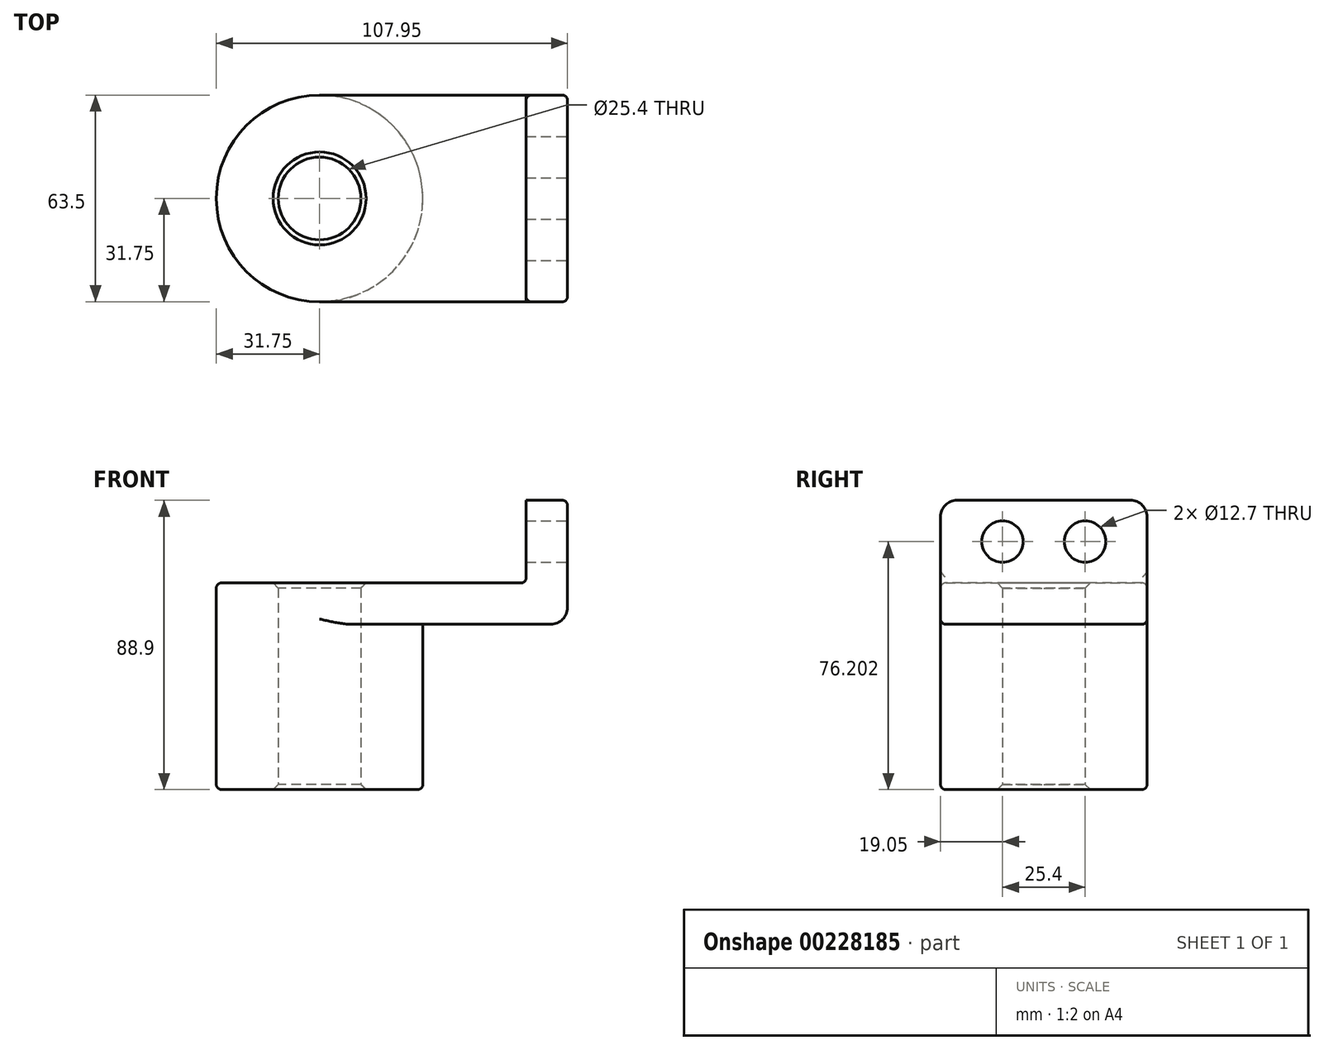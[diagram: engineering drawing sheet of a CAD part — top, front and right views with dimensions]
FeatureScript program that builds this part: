
annotation { "Feature Type Name" : "Feature", "Feature Type Description" : "" }
export const myFeature = defineFeature(function(context is Context, id is Id, definition is map)
    precondition{}
    {
        {
            var Q0;
            Q0=qCreatedBy(makeId("Top.planeOp"),FACE);
            var sketch = newSketch(context, id + "F0", { "sketchPlane" : qUnion([Q0])});
            skLineSegment(sketch, "E0.bottom", {"start": v(-38.1, 31.75) * mm, "end": v(38.1, 31.75) * mm});
            skLineSegment(sketch, "E0.top", {"start": v(-38.1, -31.75) * mm, "end": v(38.1, -31.75) * mm});
            skLineSegment(sketch, "E0.left", {"start": v(-38.1, 31.75) * mm, "end": v(-38.1, -31.75) * mm});
            skLineSegment(sketch, "E0.right", {"start": v(38.1, 31.75) * mm, "end": v(38.1, -31.75) * mm});
            skPoint(sketch, "E0.middle", {"position": v(0, 0) * mm});
            skCircle(sketch, "E1", {"center": v(-38.1, 0) * mm, "radius": 31.75 * mm});
            skCircle(sketch, "E2", {"center": v(-38.1, 0) * mm, "radius": 12.7 * mm});
            skSolve(sketch);
        }
        {
            var Q0;
            Q0 = qSketchRegion(id + "F0", true);
            extrude(context, id + "F1", {"entities" : qUnion([Q0]), "depth" : 12.7 * mm});
        }
        {
            var Q0;
            {var subQ1=sQuery(id+"F0.wireOp",EDGE,"E0.left");var subQ3=sQuery(id+"F0.wireOp",EDGE,"E2");var subQ4=makeQuery(id+"F0.imprint","INTERSECT",VERTEX,{"disambiguationData":[OD(0.0)],"derivedFrom":[subQ1,subQ3]});Q0=makeQuery(id+"F0.imprint","IMPRINT",FACE,{"disambiguationData":[TD([[makeQuery(id+"F0.imprint","IMPRINT",EDGE,{"disambiguationData":[TD([[subQ4,1.0]])],"derivedFrom":subQ3}),-1.0]])]});}
            var Q1;
            {var subQ1=sQuery(id+"F0.wireOp",EDGE,"E0.left");var subQ3=sQuery(id+"F0.wireOp",EDGE,"E2");var subQ4=makeQuery(id+"F0.imprint","INTERSECT",VERTEX,{"disambiguationData":[OD(0.0)],"derivedFrom":[subQ1,subQ3]});Q1=makeQuery(id+"F0.imprint","IMPRINT",FACE,{"disambiguationData":[TD([[makeQuery(id+"F0.imprint","IMPRINT",EDGE,{"disambiguationData":[TD([[subQ4,-1.0]])],"derivedFrom":subQ3}),-1.0]])]});}
            extrude(context, id + "F2", {"entities" : qUnion([Q0, Q1]), "operationType" : NewBodyOperationType.ADD, "oppositeDirection" : true, "depth" : 50.8 * mm});
        }
        {
            var Q0;
            Q0=makeQuery(id+"F1.opExtrude","SWEPT_FACE",FACE,{"disambiguationData":[OSD([sQuery(id+"F0.wireOp",EDGE,"E0.right")])]});
            var sketch = newSketch(context, id + "F3", { "sketchPlane" : qUnion([Q0])});
            skLineSegment(sketch, "E3.bottom", {"start": v(31.75, 0) * mm, "end": v(-31.75, 0) * mm});
            skLineSegment(sketch, "E3.top", {"start": v(31.75, 38.1) * mm, "end": v(-31.75, 38.1) * mm});
            skLineSegment(sketch, "E3.left", {"start": v(31.75, 0) * mm, "end": v(31.75, 38.1) * mm});
            skLineSegment(sketch, "E3.right", {"start": v(-31.75, 0) * mm, "end": v(-31.75, 38.1) * mm});
            skCircle(sketch, "E4", {"center": v(12.7, 25.4) * mm, "radius": 6.35 * mm});
            skLineSegment(sketch, "E5", {"start": v(0, 12.7) * mm, "end": v(0, 38.1) * mm, "construction": true});
            skCircle(sketch, "E6.MirrorC", {"center": v(-12.7, 25.4) * mm, "radius": 6.35 * mm});
            skSolve(sketch);
        }
        {
            var Q0;
            Q0 = qSketchRegion(id + "F3", true);
            extrude(context, id + "F4", {"entities" : qUnion([Q0]), "operationType" : NewBodyOperationType.ADD, "oppositeDirection" : true, "depth" : 12.7 * mm});
        }
        {
            var Q0;
            Q0=makeQuery(id+"F2.opExtrude","CAP_EDGE",EDGE,{"disambiguationData":[OSD([sQuery(id+"F0.wireOp",EDGE,"E1")])],"isStart":true});
            var Q1;
            Q1=makeQuery(id+"F1.opExtrude","CAP_EDGE",EDGE,{"disambiguationData":[OSD([sQuery(id+"F0.wireOp",EDGE,"E0.right")])],"isStart":true});
            var Q2;
            Q2=makeQuery(id+"F4.opExtrude","SWEPT_EDGE",EDGE,{"disambiguationData":[OSD([sQuery(id+"F3.wireOp",EDGE,"E3.top"),sQuery(id+"F3.wireOp",EDGE,"E3.left")])]});
            var Q3;
            Q3=makeQuery(id+"F4.opExtrude","SWEPT_EDGE",EDGE,{"disambiguationData":[OSD([sQuery(id+"F3.wireOp",EDGE,"E3.top"),sQuery(id+"F3.wireOp",EDGE,"E3.right")])]});
            fillet(context, id + "F5", {"entities" : qUnion([Q0, Q1, Q2, Q3]), "radius" : 5.08 * mm, "tangentPropagation" : true, "allowEdgeOverflow" : false});
        }
        {
            var Q0;
            Q0=makeQuery(id+"F1.opExtrude","CAP_EDGE",EDGE,{"disambiguationData":[OSD([sQuery(id+"F0.wireOp",EDGE,"E0.bottom")])],"isStart":true});
            var Q1;
            Q1=makeQuery(id+"F1.opExtrude","CAP_EDGE",EDGE,{"disambiguationData":[OSD([sQuery(id+"F0.wireOp",EDGE,"E0.bottom")])],"isStart":false});
            var Q2;
            Q2=makeQuery(id+"F4.boolean.opBoolean","INTERSECT",EDGE,{"derivedFrom":[makeQuery(id+"F1.opExtrude","CAP_FACE",FACE,{"disambiguationData":[OSD([sQuery(id+"F0.wireOp",EDGE,"E0.bottom"),sQuery(id+"F0.wireOp",EDGE,"E0.top"),sQuery(id+"F0.wireOp",EDGE,"E0.right"),sQuery(id+"F0.wireOp",EDGE,"E1"),sQuery(id+"F0.wireOp",EDGE,"E2")])],"isStart":false}),makeQuery(id+"F4.opExtrude","CAP_FACE",FACE,{"disambiguationData":[OSD([sQuery(id+"F3.wireOp",EDGE,"E3.bottom"),sQuery(id+"F3.wireOp",EDGE,"E3.top"),sQuery(id+"F3.wireOp",EDGE,"E3.left"),sQuery(id+"F3.wireOp",EDGE,"E3.right"),sQuery(id+"F3.wireOp",EDGE,"E4"),sQuery(id+"F3.wireOp",EDGE,"E6.MirrorC")])],"isStart":false})]});
            fillet(context, id + "F6", {"entities" : qUnion([Q0, Q1, Q2]), "radius" : 1.59 * mm, "tangentPropagation" : true, "allowEdgeOverflow" : false});
        }
        {
            var Q0;
            {var subQ0=sQuery(id+"F0.wireOp",EDGE,"E2");Q0=makeQuery(id+"F2.boolean.opBoolean","MERGE",FACE,{"derivedFrom":[makeQuery(id+"F1.opExtrude","SWEPT_FACE",FACE,{"disambiguationData":[OSD([subQ0])]}),makeQuery(id+"F2.opExtrude","SWEPT_FACE",FACE,{"disambiguationData":[OSD([subQ0])]})]});}
            chamfer(context, id + "F7", {"entities" : qUnion([Q0]), "width" : 1.59 * mm, "tangentPropagation" : true});
        }
        {
            var Q0;
            Q0=makeQuery(id+"F2.opExtrude","CAP_EDGE",EDGE,{"disambiguationData":[OSD([sQuery(id+"F0.wireOp",EDGE,"E1")])],"isStart":false});
            fillet(context, id + "F8", {"entities" : qUnion([Q0]), "radius" : 1.59 * mm, "tangentPropagation" : true, "allowEdgeOverflow" : false});
        }
    });
